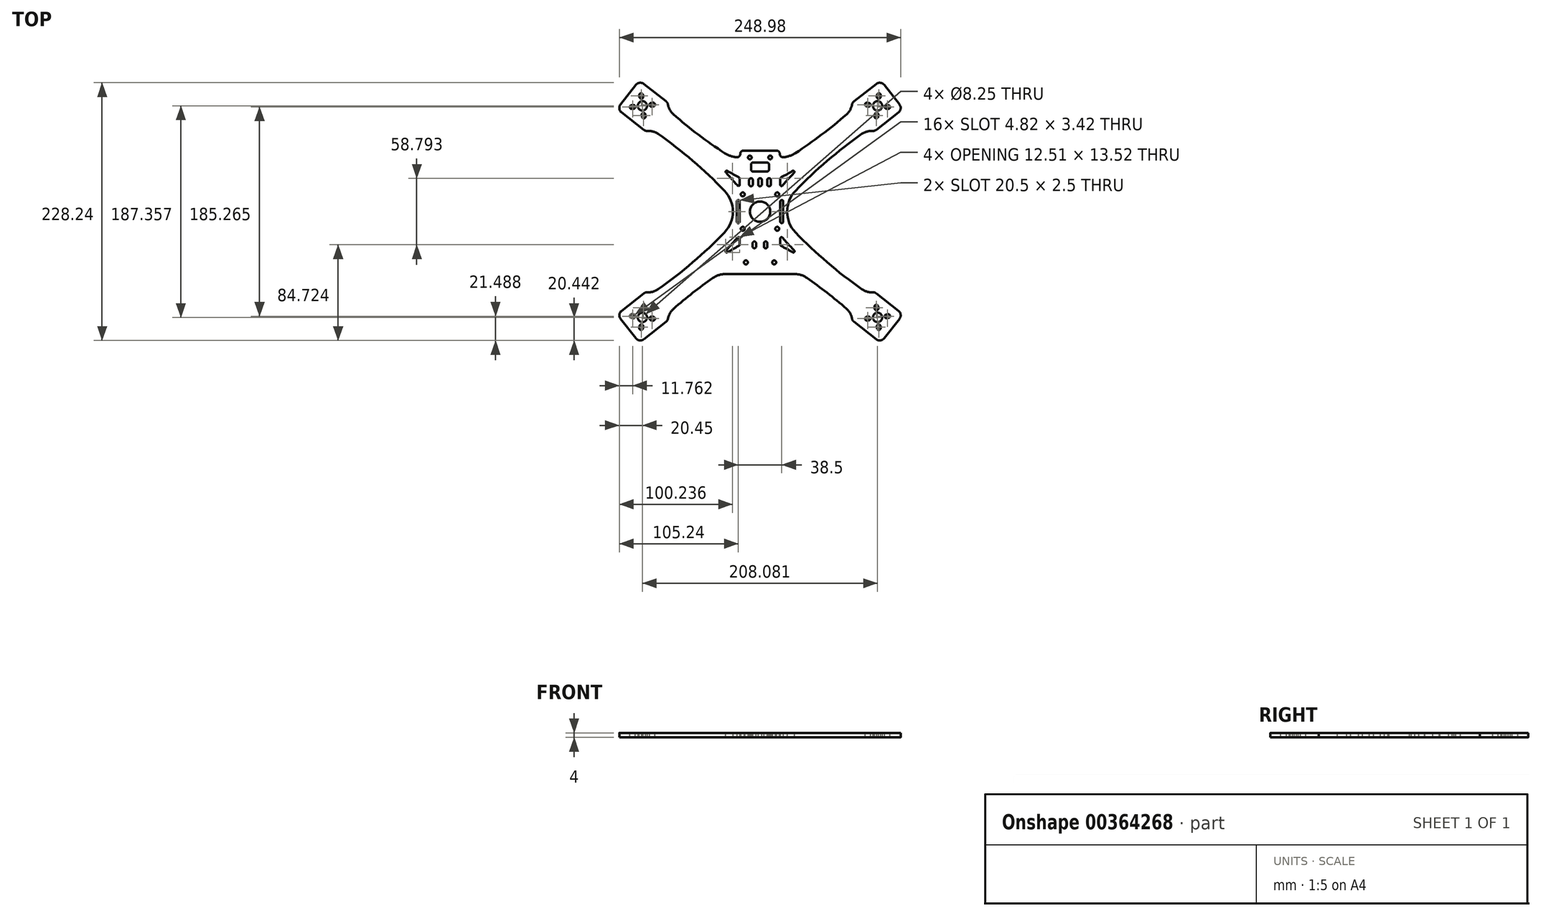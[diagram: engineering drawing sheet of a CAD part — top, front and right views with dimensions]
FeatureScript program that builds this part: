
annotation { "Feature Type Name" : "Feature", "Feature Type Description" : "" }
export const myFeature = defineFeature(function(context is Context, id is Id, definition is map)
    precondition{}
    {
        {
            var Q0;
            Q0=qCreatedBy(makeId("Top.planeOp"),FACE);
            var sketch = newSketch(context, id + "F0", { "sketchPlane" : qUnion([Q0])});
            skCircle(sketch, "E0", {"center": v(-15.25, 15.25) * mm, "radius": 1.75 * mm});
            skCircle(sketch, "E1", {"center": v(0, 0) * mm, "radius": 140 * mm, "construction": true});
            skCircle(sketch, "E2", {"center": v(-104.04, 93.68) * mm, "radius": 90 * mm, "construction": true});
            skLineSegment(sketch, "E3", {"start": v(0, 0) * mm, "end": v(-104.04, 93.68) * mm, "construction": true});
            skLineSegment(sketch, "E4", {"start": v(-104.04, 93.68) * mm, "end": v(0, 12) * mm, "construction": true});
            skLineSegment(sketch, "E5.bottom", {"start": v(-123.42, 94.9) * mm, "end": v(-109.83, 112.21) * mm});
            skLineSegment(sketch, "E5.left", {"start": v(-122.57, 87.89) * mm, "end": v(-102.95, 72.48) * mm});
            skLineSegment(sketch, "E5.right", {"start": v(-102.81, 113.06) * mm, "end": v(-83.2, 97.65) * mm});
            skLineSegment(sketch, "E6", {"start": v(-17.5, 54) * mm, "end": v(0, 54) * mm});
            skArc(sketch, "E7", {"start": v(-81.36, 94.62) * mm, "mid": v(-79.65, 89.9) * mm, "end": v(-76.48, 86.03) * mm});
            skArc(sketch, "E8", {"start": v(-90.07, 68.72) * mm, "mid": v(-94.59, 70.88) * mm, "end": v(-99.57, 71.42) * mm});
            skLineSegment(sketch, "E9", {"start": v(-19.25, 9) * mm, "end": v(-19.25, -9) * mm, "construction": true});
            skArc(sketch, "E10.0.startCap", {"start": v(-20.5, 9) * mm, "mid": v(-19.25, 10.25) * mm, "end": v(-18, 9) * mm});
            skArc(sketch, "E10.0.endCap", {"start": v(-18, -9) * mm, "mid": v(-19.25, -10.25) * mm, "end": v(-20.5, -9) * mm});
            skLineSegment(sketch, "E10.0.left", {"start": v(-18, 9) * mm, "end": v(-18, -9) * mm});
            skLineSegment(sketch, "E10.0.right", {"start": v(-20.5, 9) * mm, "end": v(-20.5, -9) * mm});
            skPoint(sketch, "E11.visualSharp", {"position": v(-126.5, 90.97) * mm});
            skArc(sketch, "E11.filletArc", {"start": v(-123.42, 94.9) * mm, "mid": v(-124.45, 91.22) * mm, "end": v(-122.57, 87.89) * mm});
            skPoint(sketch, "E12.visualSharp", {"position": v(-106.75, 116.14) * mm});
            skArc(sketch, "E12.filletArc", {"start": v(-102.81, 113.06) * mm, "mid": v(-106.5, 114.09) * mm, "end": v(-109.83, 112.21) * mm});
            skPoint(sketch, "E13.visualSharp", {"position": v(-101.34, 71.21) * mm});
            skArc(sketch, "E13.filletArc", {"start": v(-102.95, 72.48) * mm, "mid": v(-101.36, 71.64) * mm, "end": v(-99.57, 71.42) * mm});
            skPoint(sketch, "E14.visualSharp", {"position": v(-81.58, 96.38) * mm});
            skArc(sketch, "E14.filletArc", {"start": v(-81.36, 94.62) * mm, "mid": v(-82, 96.3) * mm, "end": v(-83.2, 97.65) * mm});
            skArc(sketch, "E15.MirrorCS", {"start": v(20.5, 9) * mm, "mid": v(19.25, 10.25) * mm, "end": v(18, 9) * mm});
            skArc(sketch, "E16.MirrorCS", {"start": v(81.36, 94.62) * mm, "mid": v(82, 96.3) * mm, "end": v(83.2, 97.65) * mm});
            skArc(sketch, "E17.MirrorCS", {"start": v(18, -9) * mm, "mid": v(19.25, -10.25) * mm, "end": v(20.5, -9) * mm});
            skArc(sketch, "E18.MirrorCS", {"start": v(102.95, 72.48) * mm, "mid": v(101.36, 71.64) * mm, "end": v(99.57, 71.42) * mm});
            skArc(sketch, "E19.MirrorCS", {"start": v(123.42, 94.9) * mm, "mid": v(124.45, 91.22) * mm, "end": v(122.57, 87.89) * mm});
            skArc(sketch, "E20.MirrorCS", {"start": v(81.36, 94.62) * mm, "mid": v(79.65, 89.9) * mm, "end": v(76.48, 86.03) * mm});
            skArc(sketch, "E21.MirrorCS", {"start": v(102.81, 113.06) * mm, "mid": v(106.5, 114.09) * mm, "end": v(109.83, 112.21) * mm});
            skArc(sketch, "E22.MirrorCS", {"start": v(90.07, 68.72) * mm, "mid": v(94.59, 70.88) * mm, "end": v(99.57, 71.42) * mm});
            skLineSegment(sketch, "E23.MirrorCS", {"start": v(20.5, 9) * mm, "end": v(20.5, -9) * mm});
            skLineSegment(sketch, "E24.MirrorCS", {"start": v(18, 9) * mm, "end": v(18, -9) * mm});
            skLineSegment(sketch, "E25.MirrorCS", {"start": v(19.25, 9) * mm, "end": v(19.25, -9) * mm, "construction": true});
            skLineSegment(sketch, "E26.MirrorCS", {"start": v(17.5, 54) * mm, "end": v(0, 54) * mm});
            skCircle(sketch, "E27.MirrorC", {"center": v(15.25, 15.25) * mm, "radius": 1.75 * mm});
            skPoint(sketch, "E28.MirrorP", {"position": v(81.58, 96.38) * mm});
            skLineSegment(sketch, "E29.MirrorCS", {"start": v(123.42, 94.9) * mm, "end": v(109.83, 112.21) * mm});
            skLineSegment(sketch, "E30.MirrorCS", {"start": v(0, 0) * mm, "end": v(104.04, 93.68) * mm, "construction": true});
            skLineSegment(sketch, "E31.MirrorCS", {"start": v(104.04, 93.68) * mm, "end": v(0, 12) * mm, "construction": true});
            skCircle(sketch, "E32.MirrorC", {"center": v(104.04, 93.68) * mm, "radius": 90 * mm, "construction": true});
            skLineSegment(sketch, "E33.MirrorCS", {"start": v(122.57, 87.89) * mm, "end": v(102.95, 72.48) * mm});
            skLineSegment(sketch, "E34.MirrorCS", {"start": v(102.81, 113.06) * mm, "end": v(83.2, 97.65) * mm});
            skPoint(sketch, "E35.MirrorP", {"position": v(106.75, 116.14) * mm});
            skPoint(sketch, "E36.MirrorP", {"position": v(101.34, 71.21) * mm});
            skPoint(sketch, "E37.MirrorP", {"position": v(126.5, 90.97) * mm});
            skArc(sketch, "E38.MirrorCS", {"start": v(-81.36, -94.62) * mm, "mid": v(-82, -96.3) * mm, "end": v(-83.2, -97.65) * mm});
            skArc(sketch, "E39.MirrorCS", {"start": v(-102.95, -72.48) * mm, "mid": v(-101.36, -71.64) * mm, "end": v(-99.57, -71.42) * mm});
            skArc(sketch, "E40.MirrorCS", {"start": v(81.36, -94.62) * mm, "mid": v(82, -96.3) * mm, "end": v(83.2, -97.65) * mm});
            skArc(sketch, "E41.MirrorCS", {"start": v(102.95, -72.48) * mm, "mid": v(101.36, -71.64) * mm, "end": v(99.57, -71.42) * mm});
            skArc(sketch, "E42.MirrorCS", {"start": v(90.07, -68.72) * mm, "mid": v(94.59, -70.88) * mm, "end": v(99.57, -71.42) * mm});
            skArc(sketch, "E43.MirrorCS", {"start": v(102.81, -113.06) * mm, "mid": v(106.5, -114.09) * mm, "end": v(109.83, -112.21) * mm});
            skArc(sketch, "E44.MirrorCS", {"start": v(-102.81, -113.06) * mm, "mid": v(-106.5, -114.09) * mm, "end": v(-109.83, -112.21) * mm});
            skArc(sketch, "E45.MirrorCS", {"start": v(-90.07, -68.72) * mm, "mid": v(-94.59, -70.88) * mm, "end": v(-99.57, -71.42) * mm});
            skArc(sketch, "E46.MirrorCS", {"start": v(-81.36, -94.62) * mm, "mid": v(-79.65, -89.9) * mm, "end": v(-76.48, -86.03) * mm});
            skArc(sketch, "E47.MirrorCS", {"start": v(123.42, -94.9) * mm, "mid": v(124.45, -91.22) * mm, "end": v(122.57, -87.89) * mm});
            skArc(sketch, "E48.MirrorCS", {"start": v(81.36, -94.62) * mm, "mid": v(79.65, -89.9) * mm, "end": v(76.48, -86.03) * mm});
            skArc(sketch, "E49.MirrorCS", {"start": v(-123.42, -94.9) * mm, "mid": v(-124.45, -91.22) * mm, "end": v(-122.57, -87.89) * mm});
            skCircle(sketch, "E50.MirrorC", {"center": v(-15.25, -15.25) * mm, "radius": 1.75 * mm});
            skCircle(sketch, "E51.MirrorC", {"center": v(15.25, -15.25) * mm, "radius": 1.75 * mm});
            skPoint(sketch, "E52.MirrorP", {"position": v(-81.58, -96.38) * mm});
            skLineSegment(sketch, "E53.MirrorCS", {"start": v(102.81, -113.06) * mm, "end": v(83.2, -97.65) * mm});
            skPoint(sketch, "E54.MirrorP", {"position": v(126.5, -90.97) * mm});
            skLineSegment(sketch, "E55.MirrorCS", {"start": v(122.57, -87.89) * mm, "end": v(102.95, -72.48) * mm});
            skPoint(sketch, "E56.MirrorP", {"position": v(101.34, -71.21) * mm});
            skPoint(sketch, "E57.MirrorP", {"position": v(-101.34, -71.21) * mm});
            skLineSegment(sketch, "E58.MirrorCS", {"start": v(-102.81, -113.06) * mm, "end": v(-83.2, -97.65) * mm});
            skLineSegment(sketch, "E59.MirrorCS", {"start": v(-122.57, -87.89) * mm, "end": v(-102.95, -72.48) * mm});
            skLineSegment(sketch, "E60.MirrorCS", {"start": v(-123.42, -94.9) * mm, "end": v(-109.83, -112.21) * mm});
            skPoint(sketch, "E61.MirrorP", {"position": v(-106.75, -116.14) * mm});
            skLineSegment(sketch, "E62.MirrorCS", {"start": v(123.42, -94.9) * mm, "end": v(109.83, -112.21) * mm});
            skPoint(sketch, "E63.MirrorP", {"position": v(106.75, -116.14) * mm});
            skPoint(sketch, "E64.MirrorP", {"position": v(-126.5, -90.97) * mm});
            skPoint(sketch, "E65.MirrorP", {"position": v(81.58, -96.38) * mm});
            skCircle(sketch, "E66.MirrorC", {"center": v(-104.04, -93.68) * mm, "radius": 90 * mm, "construction": true});
            skCircle(sketch, "E67.MirrorC", {"center": v(104.04, -93.68) * mm, "radius": 90 * mm, "construction": true});
            skCircle(sketch, "E68", {"center": v(-104.04, 93.68) * mm, "radius": 4.12 * mm});
            skCircle(sketch, "E69.MirrorC", {"center": v(104.04, 93.68) * mm, "radius": 4.12 * mm});
            skCircle(sketch, "E70.MirrorC", {"center": v(-104.04, -93.68) * mm, "radius": 4.12 * mm});
            skCircle(sketch, "E71.MirrorC", {"center": v(104.04, -93.68) * mm, "radius": 4.12 * mm});
            skArc(sketch, "E72", {"start": v(-31.4, 18.4) * mm, "mid": v(-59.52, 44.98) * mm, "end": v(-90.07, 68.72) * mm});
            skArc(sketch, "E73.MirrorCS", {"start": v(31.4, 18.4) * mm, "mid": v(59.52, 44.98) * mm, "end": v(90.07, 68.72) * mm});
            skArc(sketch, "E74.MirrorCS", {"start": v(-31.4, -18.4) * mm, "mid": v(-59.52, -44.98) * mm, "end": v(-90.07, -68.72) * mm});
            skArc(sketch, "E75.MirrorCS", {"start": v(31.4, -18.4) * mm, "mid": v(59.52, -44.98) * mm, "end": v(90.07, -68.72) * mm});
            skArc(sketch, "E76.trimOffspring", {"start": v(-31.27, 51.8) * mm, "mid": v(-54.48, 68.11) * mm, "end": v(-76.48, 86.03) * mm});
            skArc(sketch, "E77.MirrorCS", {"start": v(31.27, 51.8) * mm, "mid": v(54.48, 68.11) * mm, "end": v(76.48, 86.03) * mm});
            skArc(sketch, "E78.MirrorCS", {"start": v(41.71, -58.84) * mm, "mid": v(59.47, -71.95) * mm, "end": v(76.48, -86.03) * mm});
            skArc(sketch, "E79.MirrorCS", {"start": v(-41.71, -58.84) * mm, "mid": v(-59.47, -71.95) * mm, "end": v(-76.48, -86.03) * mm});
            skLineSegment(sketch, "E80", {"start": v(-30.28, -55.25) * mm, "end": v(30.28, -55.25) * mm});
            skPoint(sketch, "E81.visualSharp", {"position": v(-36.47, -55.25) * mm});
            skArc(sketch, "E81.filletArc", {"start": v(-30.28, -55.25) * mm, "mid": v(-36.27, -56.17) * mm, "end": v(-41.71, -58.84) * mm});
            skPoint(sketch, "E82.visualSharp", {"position": v(36.47, -55.25) * mm});
            skArc(sketch, "E82.filletArc", {"start": v(41.71, -58.84) * mm, "mid": v(36.27, -56.17) * mm, "end": v(30.28, -55.25) * mm});
            skArc(sketch, "E83.filletArc", {"start": v(-31.27, 51.8) * mm, "mid": v(-26.26, 49.33) * mm, "end": v(-20.8, 48.1) * mm});
            skArc(sketch, "E84.filletArc", {"start": v(20.8, 48.1) * mm, "mid": v(26.26, 49.33) * mm, "end": v(31.27, 51.8) * mm});
            skCircle(sketch, "E85", {"center": v(-9, 48) * mm, "radius": 1.63 * mm});
            skLineSegment(sketch, "E86", {"start": v(-17.5, 54) * mm, "end": v(-17.5, 51.1) * mm});
            skLineSegment(sketch, "E87", {"start": v(17.5, 54) * mm, "end": v(17.5, 51.1) * mm});
            skPoint(sketch, "E88.visualSharp", {"position": v(-17.5, 48) * mm});
            skArc(sketch, "E88.filletArc", {"start": v(-20.8, 48.1) * mm, "mid": v(-18.49, 48.86) * mm, "end": v(-17.5, 51.1) * mm});
            skPoint(sketch, "E89.visualSharp", {"position": v(17.5, 48) * mm});
            skArc(sketch, "E89.filletArc", {"start": v(17.5, 51.1) * mm, "mid": v(18.49, 48.86) * mm, "end": v(20.8, 48.1) * mm});
            skCircle(sketch, "E90.MirrorC", {"center": v(9, 48) * mm, "radius": 1.63 * mm});
            skPoint(sketch, "E91.visualSharp", {"position": v(-14.8, 0) * mm});
            skArc(sketch, "E91.filletArc", {"start": v(-31.4, -18.4) * mm, "mid": v(-24, 0) * mm, "end": v(-31.4, 18.4) * mm});
            skPoint(sketch, "E92.visualSharp", {"position": v(14.8, 0) * mm});
            skArc(sketch, "E92.filletArc", {"start": v(31.4, 18.4) * mm, "mid": v(24, 0) * mm, "end": v(31.4, -18.4) * mm});
            skCircle(sketch, "E93", {"center": v(-12.5, -45) * mm, "radius": 1.75 * mm});
            skCircle(sketch, "E94.MirrorC", {"center": v(12.5, -45) * mm, "radius": 1.75 * mm});
            skSolve(sketch);
        }
        {
            var Q0;
            Q0=qSketchRegion(id+"F0",true);
            extrude(context, id + "F1", {"entities" : qUnion([Q0]), "depth" : 4 * mm});
        }
        {
            var Q0;
            Q0=makeQuery(id+"F1.opExtrude","CAP_FACE",FACE,{"disambiguationData":[OSD([sQuery(id+"F0.wireOp",EDGE,"E0"),sQuery(id+"F0.wireOp",EDGE,"bZv11kwC-7Zwh-qoiM-MuVD-QWfY3VRXTvEb"),sQuery(id+"F0.wireOp",EDGE,"Hg7IfRWj-3ALA-Ly6Y-QmXC-kUpIx1ZQ4bFj"),sQuery(id+"F0.wireOp",EDGE,"i2Ly1i0H-hUQD-DSDW-V0AA-PaiG6Uw8rzNW"),sQuery(id+"F0.wireOp",EDGE,"E5.bottom"),sQuery(id+"F0.wireOp",EDGE,"E5.left"),sQuery(id+"F0.wireOp",EDGE,"E5.right"),sQuery(id+"F0.wireOp",EDGE,"E7"),sQuery(id+"F0.wireOp",EDGE,"E8"),sQuery(id+"F0.wireOp",EDGE,"26a3e7e2-4a16-4030-acf8-3f1fbd5a5a34.filletArc"),sQuery(id+"F0.wireOp",EDGE,"E10.0.startCap"),sQuery(id+"F0.wireOp",EDGE,"E10.0.endCap"),sQuery(id+"F0.wireOp",EDGE,"E10.0.left"),sQuery(id+"F0.wireOp",EDGE,"E10.0.right"),sQuery(id+"F0.wireOp",EDGE,"E11.filletArc"),sQuery(id+"F0.wireOp",EDGE,"E12.filletArc"),sQuery(id+"F0.wireOp",EDGE,"E13.filletArc"),sQuery(id+"F0.wireOp",EDGE,"E14.filletArc"),sQuery(id+"F0.wireOp",EDGE,"E15.MirrorCS"),sQuery(id+"F0.wireOp",EDGE,"E16.MirrorCS"),sQuery(id+"F0.wireOp",EDGE,"E17.MirrorCS"),sQuery(id+"F0.wireOp",EDGE,"E18.MirrorCS"),sQuery(id+"F0.wireOp",EDGE,"E19.MirrorCS"),sQuery(id+"F0.wireOp",EDGE,"E20.MirrorCS"),sQuery(id+"F0.wireOp",EDGE,"b7ecff87-ac14-4935-8a3e-caa413c79c2e13.MirrorCS"),sQuery(id+"F0.wireOp",EDGE,"E21.MirrorCS"),sQuery(id+"F0.wireOp",EDGE,"E22.MirrorCS"),sQuery(id+"F0.wireOp",EDGE,"E23.MirrorCS"),sQuery(id+"F0.wireOp",EDGE,"E24.MirrorCS"),sQuery(id+"F0.wireOp",EDGE,"b7ecff87-ac14-4935-8a3e-caa413c79c2e23.MirrorCS"),sQuery(id+"F0.wireOp",EDGE,"E27.MirrorC"),sQuery(id+"F0.wireOp",EDGE,"E29.MirrorCS"),sQuery(id+"F0.wireOp",EDGE,"b7ecff87-ac14-4935-8a3e-caa413c79c2e29.MirrorCS"),sQuery(id+"F0.wireOp",EDGE,"E33.MirrorCS"),sQuery(id+"F0.wireOp",EDGE,"E34.MirrorCS"),sQuery(id+"F0.wireOp",EDGE,"b7ecff87-ac14-4935-8a3e-caa413c79c2e39.MirrorCS"),sQuery(id+"F0.wireOp",EDGE,"E38.MirrorCS"),sQuery(id+"F0.wireOp",EDGE,"E39.MirrorCS"),sQuery(id+"F0.wireOp",EDGE,"E40.MirrorCS"),sQuery(id+"F0.wireOp",EDGE,"E41.MirrorCS"),sQuery(id+"F0.wireOp",EDGE,"E42.MirrorCS"),sQuery(id+"F0.wireOp",EDGE,"E43.MirrorCS"),sQuery(id+"F0.wireOp",EDGE,"E44.MirrorCS"),sQuery(id+"F0.wireOp",EDGE,"E45.MirrorCS"),sQuery(id+"F0.wireOp",EDGE,"E46.MirrorCS"),sQuery(id+"F0.wireOp",EDGE,"E47.MirrorCS"),sQuery(id+"F0.wireOp",EDGE,"E48.MirrorCS"),sQuery(id+"F0.wireOp",EDGE,"E49.MirrorCS"),sQuery(id+"F0.wireOp",EDGE,"E50.MirrorC"),sQuery(id+"F0.wireOp",EDGE,"E51.MirrorC"),sQuery(id+"F0.wireOp",EDGE,"7b8357ce-6b81-4621-bb5f-09712327f37e37.MirrorCS"),sQuery(id+"F0.wireOp",EDGE,"E53.MirrorCS"),sQuery(id+"F0.wireOp",EDGE,"E55.MirrorCS"),sQuery(id+"F0.wireOp",EDGE,"E58.MirrorCS"),sQuery(id+"F0.wireOp",EDGE,"E59.MirrorCS"),sQuery(id+"F0.wireOp",EDGE,"E60.MirrorCS"),sQuery(id+"F0.wireOp",EDGE,"7b8357ce-6b81-4621-bb5f-09712327f37e49.MirrorCS"),sQuery(id+"F0.wireOp",EDGE,"7b8357ce-6b81-4621-bb5f-09712327f37e50.MirrorCS"),sQuery(id+"F0.wireOp",EDGE,"E62.MirrorCS"),sQuery(id+"F0.wireOp",EDGE,"7b8357ce-6b81-4621-bb5f-09712327f37e55.MirrorCS"),sQuery(id+"F0.wireOp",EDGE,"d83ce2ea-2607-4b6c-a04d-38c7ae4304c90.MirrorCS"),sQuery(id+"F0.wireOp",EDGE,"b69c18a7-e43b-42be-b145-92b5204aa2ed0.MirrorCS"),sQuery(id+"F0.wireOp",EDGE,"a0707623-7043-4475-b436-6124989390590.MirrorCS"),sQuery(id+"F0.wireOp",EDGE,"4f61c261-c1ce-4229-8802-2f54477ed9b20.MirrorCS"),sQuery(id+"F0.wireOp",EDGE,"PiAP6XZh-xq8d-wj9O-Epc7-kF4WUdjTUHBz"),sQuery(id+"F0.wireOp",EDGE,"26e37ba6-caeb-4f33-ab48-1d1fe7035cbd0.MirrorC"),sQuery(id+"F0.wireOp",EDGE,"2yan8IeJ-tOHB-Kgj5-MnLH-DyiSyil4pG3S"),sQuery(id+"F0.wireOp",EDGE,"gHJ05LQx-usyR-kV3a-hPzh-QXjW5T1wXW1p"),sQuery(id+"F0.wireOp",EDGE,"uchXSoDE-KjdM-uTwm-rJXX-9rzWfyOP3x4Z"),sQuery(id+"F0.wireOp",EDGE,"8eu2Gxre-rbZ0-mDo1-W97T-pc3IviFYihye"),sQuery(id+"F0.wireOp",EDGE,"eavqlNsN-eOFr-pDPr-DEgw-YRCTYlhg5u3t"),sQuery(id+"F0.wireOp",EDGE,"Bw8slYh4-NEub-OYFD-4ET6-0dd0G63bUOwi"),sQuery(id+"F0.wireOp",EDGE,"af94888a-cba0-45cd-aecc-a0270221dd82.trimOffspring"),sQuery(id+"F0.wireOp",EDGE,"36199e4a-d6a7-49c4-a502-27b3488fd5e6.filletArc"),sQuery(id+"F0.wireOp",EDGE,"9e30e6b1-65ef-4937-9bd8-18fed2c5f1090.MirrorCS"),sQuery(id+"F0.wireOp",EDGE,"31f30485-6f3e-4795-917b-55e225d339680.MirrorCS"),sQuery(id+"F0.wireOp",EDGE,"86aa6092-d3c3-42aa-99ce-90435510c5960.MirrorCS"),sQuery(id+"F0.wireOp",EDGE,"5a69975c-1d9b-4b23-809c-878e26df679d0.MirrorCS"),sQuery(id+"F0.wireOp",EDGE,"8025df49-7d22-4dba-957a-6396c4b11ce90.MirrorCS"),sQuery(id+"F0.wireOp",EDGE,"b23088bf-ab4c-4e44-9a43-da8ffa8499a00.MirrorCS"),sQuery(id+"F0.wireOp",EDGE,"d9780cfa-9ead-4347-a629-1b1a594d6e410.MirrorCS"),sQuery(id+"F0.wireOp",EDGE,"68fec51b-96b4-4918-b858-b07c475e679e0.MirrorCS"),sQuery(id+"F0.wireOp",EDGE,"b72a6ee6-5ab0-4ed6-be8f-ffada714514d0.MirrorCS"),sQuery(id+"F0.wireOp",EDGE,"8773bbf2-5ef2-485a-bde0-34addb67332b0.MirrorCS"),sQuery(id+"F0.wireOp",EDGE,"ce348970-fad1-4eb4-9c27-5204bf570fdb0.MirrorCS"),sQuery(id+"F0.wireOp",EDGE,"404c4f6d-7f85-4f91-8924-7a461248f6590.MirrorCS"),sQuery(id+"F0.wireOp",EDGE,"TJ6xSgkY-RBVc-ApbF-Rnxn-nYxT4uNRJTxX"),sQuery(id+"F0.wireOp",EDGE,"hn5H7zRm-rU73-VfAX-dvYv-k9Lax7dM8k8G"),sQuery(id+"F0.wireOp",EDGE,"UOzbpYJr-Rpqu-ZeE8-tXKC-t89DSqlBGB8Q"),sQuery(id+"F0.wireOp",EDGE,"YxJJHRqV-amlc-LN3y-haml-tisoirnnfRJY"),sQuery(id+"F0.wireOp",EDGE,"033e0fe7-d3c1-42f5-ae8f-adbb043379e8.filletArc"),sQuery(id+"F0.wireOp",EDGE,"afa99035-e99d-4a73-974f-5500cdf2138a.filletArc"),sQuery(id+"F0.wireOp",EDGE,"9i3ea3iE-3Dll-Ek6R-PhGe-V1XcnAEkodY1.bottom"),sQuery(id+"F0.wireOp",EDGE,"9i3ea3iE-3Dll-Ek6R-PhGe-V1XcnAEkodY1.left"),sQuery(id+"F0.wireOp",EDGE,"9i3ea3iE-3Dll-Ek6R-PhGe-V1XcnAEkodY1.right"),sQuery(id+"F0.wireOp",EDGE,"1382622d-cae2-4c61-9f5c-b8746732d9fe0.MirrorCS"),sQuery(id+"F0.wireOp",EDGE,"0d70f9a0-c1ad-434e-a495-165a5a764f960.MirrorCS"),sQuery(id+"F0.wireOp",EDGE,"1f8d5036-162d-4fc3-b441-7a8ab5cd179e0.MirrorCS"),sQuery(id+"F0.wireOp",EDGE,"Km0E7gO1-P8tX-SnyZ-vo1L-W35BEzFtr7vK"),sQuery(id+"F0.wireOp",EDGE,"4twT0r3F-PA9R-wz1e-iyg0-9RBk79VGwi7g"),sQuery(id+"F0.wireOp",EDGE,"14bccf5c-bb99-48c5-a73f-577480a40b4e0.MirrorCS"),sQuery(id+"F0.wireOp",EDGE,"a123c59d-a695-4b06-9137-5aaff9e2b4be0.MirrorCS"),sQuery(id+"F0.wireOp",EDGE,"E68"),sQuery(id+"F0.wireOp",EDGE,"E69.MirrorC"),sQuery(id+"F0.wireOp",EDGE,"E70.MirrorC"),sQuery(id+"F0.wireOp",EDGE,"E71.MirrorC")])],"isStart":false});
            var sketch = newSketch(context, id + "F2", { "sketchPlane" : qUnion([Q0])});
            skCircle(sketch, "E95", {"center": v(-104.04, 93.68) * mm, "radius": 7.95 * mm, "construction": true});
            skCircle(sketch, "E96", {"center": v(-104.04, 93.68) * mm, "radius": 9.55 * mm, "construction": true});
            skLineSegment(sketch, "E97", {"start": v(-105, 101.57) * mm, "end": v(-105.18, 103.16) * mm, "construction": true});
            skLineSegment(sketch, "E98", {"start": v(-105, 101.57) * mm, "end": v(-104.04, 93.68) * mm, "construction": true});
            skLineSegment(sketch, "E99", {"start": v(-104.04, 93.68) * mm, "end": v(0, 12) * mm, "construction": true});
            skArc(sketch, "E100.0.startCap", {"start": v(-103.38, 101.77) * mm, "mid": v(-104.8, 99.96) * mm, "end": v(-106.6, 101.38) * mm});
            skArc(sketch, "E100.0.endCap", {"start": v(-106.8, 102.97) * mm, "mid": v(-105.38, 104.77) * mm, "end": v(-103.57, 103.35) * mm});
            skLineSegment(sketch, "E100.0.left", {"start": v(-106.6, 101.38) * mm, "end": v(-106.8, 102.97) * mm});
            skLineSegment(sketch, "E100.0.right", {"start": v(-103.38, 101.77) * mm, "end": v(-103.57, 103.35) * mm});
            skLineSegment(sketch, "E101.1.0", {"start": v(-111.93, 92.73) * mm, "end": v(-113.52, 92.54) * mm, "construction": true});
            skArc(sketch, "E101.1.1", {"start": v(-112.13, 94.34) * mm, "mid": v(-110.32, 92.92) * mm, "end": v(-111.74, 91.11) * mm});
            skLineSegment(sketch, "E101.1.2", {"start": v(-111.74, 91.11) * mm, "end": v(-113.33, 90.92) * mm});
            skLineSegment(sketch, "E101.1.3", {"start": v(-112.13, 94.34) * mm, "end": v(-113.72, 94.15) * mm});
            skArc(sketch, "E101.1.4", {"start": v(-113.33, 90.92) * mm, "mid": v(-115.14, 92.34) * mm, "end": v(-113.72, 94.15) * mm});
            skLineSegment(sketch, "E101.2.0", {"start": v(-103.09, 85.79) * mm, "end": v(-102.9, 84.2) * mm, "construction": true});
            skArc(sketch, "E101.2.1", {"start": v(-104.7, 85.6) * mm, "mid": v(-103.28, 87.4) * mm, "end": v(-101.48, 85.98) * mm});
            skLineSegment(sketch, "E101.2.2", {"start": v(-101.48, 85.98) * mm, "end": v(-101.29, 84.4) * mm});
            skLineSegment(sketch, "E101.2.3", {"start": v(-104.7, 85.6) * mm, "end": v(-104.51, 84) * mm});
            skArc(sketch, "E101.2.4", {"start": v(-101.29, 84.4) * mm, "mid": v(-102.7, 82.58) * mm, "end": v(-104.51, 84) * mm});
            skLineSegment(sketch, "E101.3.0", {"start": v(-96.15, 94.63) * mm, "end": v(-94.56, 94.82) * mm, "construction": true});
            skArc(sketch, "E101.3.1", {"start": v(-95.95, 93.02) * mm, "mid": v(-97.76, 94.43) * mm, "end": v(-96.34, 96.24) * mm});
            skLineSegment(sketch, "E101.3.2", {"start": v(-96.34, 96.24) * mm, "end": v(-94.75, 96.43) * mm});
            skLineSegment(sketch, "E101.3.3", {"start": v(-95.95, 93.02) * mm, "end": v(-94.36, 93.2) * mm});
            skArc(sketch, "E101.3.4", {"start": v(-94.75, 96.43) * mm, "mid": v(-92.95, 95.01) * mm, "end": v(-94.36, 93.2) * mm});
            skLineSegment(sketch, "E102.MirrorCS", {"start": v(105, 101.57) * mm, "end": v(105.18, 103.16) * mm, "construction": true});
            skLineSegment(sketch, "E103.MirrorCS", {"start": v(103.38, 101.77) * mm, "end": v(103.57, 103.35) * mm});
            skLineSegment(sketch, "E104.MirrorCS", {"start": v(111.93, 92.73) * mm, "end": v(113.52, 92.54) * mm, "construction": true});
            skLineSegment(sketch, "E105.MirrorCS", {"start": v(112.13, 94.34) * mm, "end": v(113.72, 94.15) * mm});
            skLineSegment(sketch, "E106.MirrorCS", {"start": v(96.34, 96.24) * mm, "end": v(94.75, 96.43) * mm});
            skLineSegment(sketch, "E107.MirrorCS", {"start": v(106.6, 101.38) * mm, "end": v(106.8, 102.97) * mm});
            skLineSegment(sketch, "E108.MirrorCS", {"start": v(104.7, 85.6) * mm, "end": v(104.51, 84) * mm});
            skLineSegment(sketch, "E109.MirrorCS", {"start": v(95.95, 93.02) * mm, "end": v(94.36, 93.2) * mm});
            skArc(sketch, "E110.MirrorCS", {"start": v(112.13, 94.34) * mm, "mid": v(110.32, 92.92) * mm, "end": v(111.74, 91.11) * mm});
            skArc(sketch, "E111.MirrorCS", {"start": v(106.8, 102.97) * mm, "mid": v(105.38, 104.77) * mm, "end": v(103.57, 103.35) * mm});
            skArc(sketch, "E112.MirrorCS", {"start": v(101.29, 84.4) * mm, "mid": v(102.7, 82.58) * mm, "end": v(104.51, 84) * mm});
            skLineSegment(sketch, "E113.MirrorCS", {"start": v(103.09, 85.79) * mm, "end": v(102.9, 84.2) * mm, "construction": true});
            skArc(sketch, "E114.MirrorCS", {"start": v(94.75, 96.43) * mm, "mid": v(92.95, 95.01) * mm, "end": v(94.36, 93.2) * mm});
            skArc(sketch, "E115.MirrorCS", {"start": v(113.33, 90.92) * mm, "mid": v(115.14, 92.34) * mm, "end": v(113.72, 94.15) * mm});
            skLineSegment(sketch, "E116.MirrorCS", {"start": v(96.15, 94.63) * mm, "end": v(94.56, 94.82) * mm, "construction": true});
            skLineSegment(sketch, "E117.MirrorCS", {"start": v(111.74, 91.11) * mm, "end": v(113.33, 90.92) * mm});
            skArc(sketch, "E118.MirrorCS", {"start": v(104.7, 85.6) * mm, "mid": v(103.28, 87.4) * mm, "end": v(101.48, 85.98) * mm});
            skArc(sketch, "E119.MirrorCS", {"start": v(95.95, 93.02) * mm, "mid": v(97.76, 94.43) * mm, "end": v(96.34, 96.24) * mm});
            skLineSegment(sketch, "E120.MirrorCS", {"start": v(101.48, 85.98) * mm, "end": v(101.29, 84.4) * mm});
            skArc(sketch, "E121.MirrorCS", {"start": v(103.38, 101.77) * mm, "mid": v(104.8, 99.96) * mm, "end": v(106.6, 101.38) * mm});
            skPoint(sketch, "E122.MirrorP", {"position": v(104.04, 93.68) * mm});
            skCircle(sketch, "E123.MirrorC", {"center": v(104.04, 93.68) * mm, "radius": 9.55 * mm, "construction": true});
            skCircle(sketch, "E124.MirrorC", {"center": v(104.04, 93.68) * mm, "radius": 7.95 * mm, "construction": true});
            skLineSegment(sketch, "E125.MirrorCS", {"start": v(105, 101.57) * mm, "end": v(104.04, 93.68) * mm, "construction": true});
            skLineSegment(sketch, "E126.MirrorCS", {"start": v(-105, -101.57) * mm, "end": v(-105.18, -103.16) * mm, "construction": true});
            skLineSegment(sketch, "E127.MirrorCS", {"start": v(-103.38, -101.77) * mm, "end": v(-103.57, -103.35) * mm});
            skArc(sketch, "E128.MirrorCS", {"start": v(-103.38, -101.77) * mm, "mid": v(-104.8, -99.96) * mm, "end": v(-106.6, -101.38) * mm});
            skLineSegment(sketch, "E129.MirrorCS", {"start": v(-105, -101.57) * mm, "end": v(-104.04, -93.68) * mm, "construction": true});
            skLineSegment(sketch, "E130.MirrorCS", {"start": v(-106.6, -101.38) * mm, "end": v(-106.8, -102.97) * mm});
            skLineSegment(sketch, "E131.MirrorCS", {"start": v(-112.13, -94.34) * mm, "end": v(-113.72, -94.15) * mm});
            skLineSegment(sketch, "E132.MirrorCS", {"start": v(95.95, -93.02) * mm, "end": v(94.36, -93.2) * mm});
            skArc(sketch, "E133.MirrorCS", {"start": v(95.95, -93.02) * mm, "mid": v(97.76, -94.43) * mm, "end": v(96.34, -96.24) * mm});
            skLineSegment(sketch, "E134.MirrorCS", {"start": v(106.6, -101.38) * mm, "end": v(106.8, -102.97) * mm});
            skArc(sketch, "E135.MirrorCS", {"start": v(-112.13, -94.34) * mm, "mid": v(-110.32, -92.92) * mm, "end": v(-111.74, -91.11) * mm});
            skLineSegment(sketch, "E136.MirrorCS", {"start": v(-111.74, -91.11) * mm, "end": v(-113.33, -90.92) * mm});
            skLineSegment(sketch, "E137.MirrorCS", {"start": v(-111.93, -92.73) * mm, "end": v(-113.52, -92.54) * mm, "construction": true});
            skArc(sketch, "E138.MirrorCS", {"start": v(-113.33, -90.92) * mm, "mid": v(-115.14, -92.34) * mm, "end": v(-113.72, -94.15) * mm});
            skLineSegment(sketch, "E139.MirrorCS", {"start": v(111.93, -92.73) * mm, "end": v(113.52, -92.54) * mm, "construction": true});
            skLineSegment(sketch, "E140.MirrorCS", {"start": v(96.15, -94.63) * mm, "end": v(94.56, -94.82) * mm, "construction": true});
            skLineSegment(sketch, "E141.MirrorCS", {"start": v(111.74, -91.11) * mm, "end": v(113.33, -90.92) * mm});
            skArc(sketch, "E142.MirrorCS", {"start": v(112.13, -94.34) * mm, "mid": v(110.32, -92.92) * mm, "end": v(111.74, -91.11) * mm});
            skLineSegment(sketch, "E143.MirrorCS", {"start": v(96.34, -96.24) * mm, "end": v(94.75, -96.43) * mm});
            skArc(sketch, "E144.MirrorCS", {"start": v(103.38, -101.77) * mm, "mid": v(104.8, -99.96) * mm, "end": v(106.6, -101.38) * mm});
            skLineSegment(sketch, "E145.MirrorCS", {"start": v(103.38, -101.77) * mm, "end": v(103.57, -103.35) * mm});
            skLineSegment(sketch, "E146.MirrorCS", {"start": v(112.13, -94.34) * mm, "end": v(113.72, -94.15) * mm});
            skArc(sketch, "E147.MirrorCS", {"start": v(113.33, -90.92) * mm, "mid": v(115.14, -92.34) * mm, "end": v(113.72, -94.15) * mm});
            skLineSegment(sketch, "E148.MirrorCS", {"start": v(105, -101.57) * mm, "end": v(104.04, -93.68) * mm, "construction": true});
            skLineSegment(sketch, "E149.MirrorCS", {"start": v(105, -101.57) * mm, "end": v(105.18, -103.16) * mm, "construction": true});
            skLineSegment(sketch, "E150.MirrorCS", {"start": v(101.48, -85.98) * mm, "end": v(101.29, -84.4) * mm});
            skLineSegment(sketch, "E151.MirrorCS", {"start": v(-101.48, -85.98) * mm, "end": v(-101.29, -84.4) * mm});
            skLineSegment(sketch, "E152.MirrorCS", {"start": v(-104.7, -85.6) * mm, "end": v(-104.51, -84) * mm});
            skArc(sketch, "E153.MirrorCS", {"start": v(-94.75, -96.43) * mm, "mid": v(-92.95, -95.01) * mm, "end": v(-94.36, -93.2) * mm});
            skArc(sketch, "E154.MirrorCS", {"start": v(106.8, -102.97) * mm, "mid": v(105.38, -104.77) * mm, "end": v(103.57, -103.35) * mm});
            skArc(sketch, "E155.MirrorCS", {"start": v(104.7, -85.6) * mm, "mid": v(103.28, -87.4) * mm, "end": v(101.48, -85.98) * mm});
            skArc(sketch, "E156.MirrorCS", {"start": v(-101.29, -84.4) * mm, "mid": v(-102.7, -82.58) * mm, "end": v(-104.51, -84) * mm});
            skLineSegment(sketch, "E157.MirrorCS", {"start": v(-96.34, -96.24) * mm, "end": v(-94.75, -96.43) * mm});
            skArc(sketch, "E158.MirrorCS", {"start": v(-95.95, -93.02) * mm, "mid": v(-97.76, -94.43) * mm, "end": v(-96.34, -96.24) * mm});
            skArc(sketch, "E159.MirrorCS", {"start": v(-106.8, -102.97) * mm, "mid": v(-105.38, -104.77) * mm, "end": v(-103.57, -103.35) * mm});
            skArc(sketch, "E160.MirrorCS", {"start": v(101.29, -84.4) * mm, "mid": v(102.7, -82.58) * mm, "end": v(104.51, -84) * mm});
            skLineSegment(sketch, "E161.MirrorCS", {"start": v(-96.15, -94.63) * mm, "end": v(-94.56, -94.82) * mm, "construction": true});
            skArc(sketch, "E162.MirrorCS", {"start": v(94.75, -96.43) * mm, "mid": v(92.95, -95.01) * mm, "end": v(94.36, -93.2) * mm});
            skArc(sketch, "E163.MirrorCS", {"start": v(-104.7, -85.6) * mm, "mid": v(-103.28, -87.4) * mm, "end": v(-101.48, -85.98) * mm});
            skLineSegment(sketch, "E164.MirrorCS", {"start": v(-95.95, -93.02) * mm, "end": v(-94.36, -93.2) * mm});
            skLineSegment(sketch, "E165.MirrorCS", {"start": v(104.7, -85.6) * mm, "end": v(104.51, -84) * mm});
            skLineSegment(sketch, "E166.MirrorCS", {"start": v(103.09, -85.79) * mm, "end": v(102.9, -84.2) * mm, "construction": true});
            skLineSegment(sketch, "E167.MirrorCS", {"start": v(-103.09, -85.79) * mm, "end": v(-102.9, -84.2) * mm, "construction": true});
            skCircle(sketch, "E168.MirrorC", {"center": v(104.04, -93.68) * mm, "radius": 7.95 * mm, "construction": true});
            skCircle(sketch, "E169.MirrorC", {"center": v(-104.04, -93.68) * mm, "radius": 7.95 * mm, "construction": true});
            skCircle(sketch, "E170.MirrorC", {"center": v(-104.04, -93.68) * mm, "radius": 9.55 * mm, "construction": true});
            skCircle(sketch, "E171.MirrorC", {"center": v(104.04, -93.68) * mm, "radius": 9.55 * mm, "construction": true});
            skSolve(sketch);
        }
        {
            var Q0;
            Q0=qSketchRegion(id+"F2",true);
            extrude(context, id + "F3", {"entities" : qUnion([Q0]), "operationType" : NewBodyOperationType.REMOVE, "oppositeDirection" : true, "depth" : 25 * mm, "offsetDistance" : 25 * mm});
        }
        {
            var Q0;
            Q0=makeQuery(id+"F1.opExtrude","CAP_FACE",FACE,{"disambiguationData":[OSD([sQuery(id+"F0.wireOp",EDGE,"E0"),sQuery(id+"F0.wireOp",EDGE,"bZv11kwC-7Zwh-qoiM-MuVD-QWfY3VRXTvEb"),sQuery(id+"F0.wireOp",EDGE,"Hg7IfRWj-3ALA-Ly6Y-QmXC-kUpIx1ZQ4bFj"),sQuery(id+"F0.wireOp",EDGE,"i2Ly1i0H-hUQD-DSDW-V0AA-PaiG6Uw8rzNW"),sQuery(id+"F0.wireOp",EDGE,"E5.bottom"),sQuery(id+"F0.wireOp",EDGE,"E5.left"),sQuery(id+"F0.wireOp",EDGE,"E5.right"),sQuery(id+"F0.wireOp",EDGE,"E7"),sQuery(id+"F0.wireOp",EDGE,"E8"),sQuery(id+"F0.wireOp",EDGE,"26a3e7e2-4a16-4030-acf8-3f1fbd5a5a34.filletArc"),sQuery(id+"F0.wireOp",EDGE,"E10.0.startCap"),sQuery(id+"F0.wireOp",EDGE,"E10.0.endCap"),sQuery(id+"F0.wireOp",EDGE,"E10.0.left"),sQuery(id+"F0.wireOp",EDGE,"E10.0.right"),sQuery(id+"F0.wireOp",EDGE,"E11.filletArc"),sQuery(id+"F0.wireOp",EDGE,"E12.filletArc"),sQuery(id+"F0.wireOp",EDGE,"E13.filletArc"),sQuery(id+"F0.wireOp",EDGE,"E14.filletArc"),sQuery(id+"F0.wireOp",EDGE,"E15.MirrorCS"),sQuery(id+"F0.wireOp",EDGE,"E16.MirrorCS"),sQuery(id+"F0.wireOp",EDGE,"E17.MirrorCS"),sQuery(id+"F0.wireOp",EDGE,"E18.MirrorCS"),sQuery(id+"F0.wireOp",EDGE,"E19.MirrorCS"),sQuery(id+"F0.wireOp",EDGE,"E20.MirrorCS"),sQuery(id+"F0.wireOp",EDGE,"b7ecff87-ac14-4935-8a3e-caa413c79c2e13.MirrorCS"),sQuery(id+"F0.wireOp",EDGE,"E21.MirrorCS"),sQuery(id+"F0.wireOp",EDGE,"E22.MirrorCS"),sQuery(id+"F0.wireOp",EDGE,"E23.MirrorCS"),sQuery(id+"F0.wireOp",EDGE,"E24.MirrorCS"),sQuery(id+"F0.wireOp",EDGE,"b7ecff87-ac14-4935-8a3e-caa413c79c2e23.MirrorCS"),sQuery(id+"F0.wireOp",EDGE,"E27.MirrorC"),sQuery(id+"F0.wireOp",EDGE,"E29.MirrorCS"),sQuery(id+"F0.wireOp",EDGE,"b7ecff87-ac14-4935-8a3e-caa413c79c2e29.MirrorCS"),sQuery(id+"F0.wireOp",EDGE,"E33.MirrorCS"),sQuery(id+"F0.wireOp",EDGE,"E34.MirrorCS"),sQuery(id+"F0.wireOp",EDGE,"b7ecff87-ac14-4935-8a3e-caa413c79c2e39.MirrorCS"),sQuery(id+"F0.wireOp",EDGE,"E38.MirrorCS"),sQuery(id+"F0.wireOp",EDGE,"E39.MirrorCS"),sQuery(id+"F0.wireOp",EDGE,"E40.MirrorCS"),sQuery(id+"F0.wireOp",EDGE,"E41.MirrorCS"),sQuery(id+"F0.wireOp",EDGE,"E42.MirrorCS"),sQuery(id+"F0.wireOp",EDGE,"E43.MirrorCS"),sQuery(id+"F0.wireOp",EDGE,"E44.MirrorCS"),sQuery(id+"F0.wireOp",EDGE,"E45.MirrorCS"),sQuery(id+"F0.wireOp",EDGE,"E46.MirrorCS"),sQuery(id+"F0.wireOp",EDGE,"E47.MirrorCS"),sQuery(id+"F0.wireOp",EDGE,"E48.MirrorCS"),sQuery(id+"F0.wireOp",EDGE,"E49.MirrorCS"),sQuery(id+"F0.wireOp",EDGE,"E50.MirrorC"),sQuery(id+"F0.wireOp",EDGE,"E51.MirrorC"),sQuery(id+"F0.wireOp",EDGE,"7b8357ce-6b81-4621-bb5f-09712327f37e37.MirrorCS"),sQuery(id+"F0.wireOp",EDGE,"E53.MirrorCS"),sQuery(id+"F0.wireOp",EDGE,"E55.MirrorCS"),sQuery(id+"F0.wireOp",EDGE,"E58.MirrorCS"),sQuery(id+"F0.wireOp",EDGE,"E59.MirrorCS"),sQuery(id+"F0.wireOp",EDGE,"E60.MirrorCS"),sQuery(id+"F0.wireOp",EDGE,"7b8357ce-6b81-4621-bb5f-09712327f37e49.MirrorCS"),sQuery(id+"F0.wireOp",EDGE,"7b8357ce-6b81-4621-bb5f-09712327f37e50.MirrorCS"),sQuery(id+"F0.wireOp",EDGE,"E62.MirrorCS"),sQuery(id+"F0.wireOp",EDGE,"7b8357ce-6b81-4621-bb5f-09712327f37e55.MirrorCS"),sQuery(id+"F0.wireOp",EDGE,"d83ce2ea-2607-4b6c-a04d-38c7ae4304c90.MirrorCS"),sQuery(id+"F0.wireOp",EDGE,"b69c18a7-e43b-42be-b145-92b5204aa2ed0.MirrorCS"),sQuery(id+"F0.wireOp",EDGE,"a0707623-7043-4475-b436-6124989390590.MirrorCS"),sQuery(id+"F0.wireOp",EDGE,"4f61c261-c1ce-4229-8802-2f54477ed9b20.MirrorCS"),sQuery(id+"F0.wireOp",EDGE,"PiAP6XZh-xq8d-wj9O-Epc7-kF4WUdjTUHBz"),sQuery(id+"F0.wireOp",EDGE,"26e37ba6-caeb-4f33-ab48-1d1fe7035cbd0.MirrorC"),sQuery(id+"F0.wireOp",EDGE,"2yan8IeJ-tOHB-Kgj5-MnLH-DyiSyil4pG3S"),sQuery(id+"F0.wireOp",EDGE,"gHJ05LQx-usyR-kV3a-hPzh-QXjW5T1wXW1p"),sQuery(id+"F0.wireOp",EDGE,"uchXSoDE-KjdM-uTwm-rJXX-9rzWfyOP3x4Z"),sQuery(id+"F0.wireOp",EDGE,"8eu2Gxre-rbZ0-mDo1-W97T-pc3IviFYihye"),sQuery(id+"F0.wireOp",EDGE,"eavqlNsN-eOFr-pDPr-DEgw-YRCTYlhg5u3t"),sQuery(id+"F0.wireOp",EDGE,"Bw8slYh4-NEub-OYFD-4ET6-0dd0G63bUOwi"),sQuery(id+"F0.wireOp",EDGE,"af94888a-cba0-45cd-aecc-a0270221dd82.trimOffspring"),sQuery(id+"F0.wireOp",EDGE,"36199e4a-d6a7-49c4-a502-27b3488fd5e6.filletArc"),sQuery(id+"F0.wireOp",EDGE,"9e30e6b1-65ef-4937-9bd8-18fed2c5f1090.MirrorCS"),sQuery(id+"F0.wireOp",EDGE,"31f30485-6f3e-4795-917b-55e225d339680.MirrorCS"),sQuery(id+"F0.wireOp",EDGE,"86aa6092-d3c3-42aa-99ce-90435510c5960.MirrorCS"),sQuery(id+"F0.wireOp",EDGE,"5a69975c-1d9b-4b23-809c-878e26df679d0.MirrorCS"),sQuery(id+"F0.wireOp",EDGE,"8025df49-7d22-4dba-957a-6396c4b11ce90.MirrorCS"),sQuery(id+"F0.wireOp",EDGE,"b23088bf-ab4c-4e44-9a43-da8ffa8499a00.MirrorCS"),sQuery(id+"F0.wireOp",EDGE,"d9780cfa-9ead-4347-a629-1b1a594d6e410.MirrorCS"),sQuery(id+"F0.wireOp",EDGE,"68fec51b-96b4-4918-b858-b07c475e679e0.MirrorCS"),sQuery(id+"F0.wireOp",EDGE,"b72a6ee6-5ab0-4ed6-be8f-ffada714514d0.MirrorCS"),sQuery(id+"F0.wireOp",EDGE,"8773bbf2-5ef2-485a-bde0-34addb67332b0.MirrorCS"),sQuery(id+"F0.wireOp",EDGE,"ce348970-fad1-4eb4-9c27-5204bf570fdb0.MirrorCS"),sQuery(id+"F0.wireOp",EDGE,"404c4f6d-7f85-4f91-8924-7a461248f6590.MirrorCS"),sQuery(id+"F0.wireOp",EDGE,"TJ6xSgkY-RBVc-ApbF-Rnxn-nYxT4uNRJTxX"),sQuery(id+"F0.wireOp",EDGE,"hn5H7zRm-rU73-VfAX-dvYv-k9Lax7dM8k8G"),sQuery(id+"F0.wireOp",EDGE,"UOzbpYJr-Rpqu-ZeE8-tXKC-t89DSqlBGB8Q"),sQuery(id+"F0.wireOp",EDGE,"YxJJHRqV-amlc-LN3y-haml-tisoirnnfRJY"),sQuery(id+"F0.wireOp",EDGE,"033e0fe7-d3c1-42f5-ae8f-adbb043379e8.filletArc"),sQuery(id+"F0.wireOp",EDGE,"afa99035-e99d-4a73-974f-5500cdf2138a.filletArc"),sQuery(id+"F0.wireOp",EDGE,"9i3ea3iE-3Dll-Ek6R-PhGe-V1XcnAEkodY1.bottom"),sQuery(id+"F0.wireOp",EDGE,"9i3ea3iE-3Dll-Ek6R-PhGe-V1XcnAEkodY1.left"),sQuery(id+"F0.wireOp",EDGE,"9i3ea3iE-3Dll-Ek6R-PhGe-V1XcnAEkodY1.right"),sQuery(id+"F0.wireOp",EDGE,"1382622d-cae2-4c61-9f5c-b8746732d9fe0.MirrorCS"),sQuery(id+"F0.wireOp",EDGE,"0d70f9a0-c1ad-434e-a495-165a5a764f960.MirrorCS"),sQuery(id+"F0.wireOp",EDGE,"1f8d5036-162d-4fc3-b441-7a8ab5cd179e0.MirrorCS"),sQuery(id+"F0.wireOp",EDGE,"Km0E7gO1-P8tX-SnyZ-vo1L-W35BEzFtr7vK"),sQuery(id+"F0.wireOp",EDGE,"4twT0r3F-PA9R-wz1e-iyg0-9RBk79VGwi7g"),sQuery(id+"F0.wireOp",EDGE,"14bccf5c-bb99-48c5-a73f-577480a40b4e0.MirrorCS"),sQuery(id+"F0.wireOp",EDGE,"a123c59d-a695-4b06-9137-5aaff9e2b4be0.MirrorCS"),sQuery(id+"F0.wireOp",EDGE,"E68"),sQuery(id+"F0.wireOp",EDGE,"E69.MirrorC"),sQuery(id+"F0.wireOp",EDGE,"E70.MirrorC"),sQuery(id+"F0.wireOp",EDGE,"E71.MirrorC")])],"isStart":false});
            var sketch = newSketch(context, id + "F4", { "sketchPlane" : qUnion([Q0])});
            skLineSegment(sketch, "E172", {"start": v(0, 28) * mm, "end": v(0, 24) * mm, "construction": true});
            skLineSegment(sketch, "E173", {"start": v(-8, 28) * mm, "end": v(-8, 24) * mm, "construction": true});
            skLineSegment(sketch, "E174.MirrorCS", {"start": v(8, 28) * mm, "end": v(8, 24) * mm, "construction": true});
            skArc(sketch, "E175.0.startCap", {"start": v(-9.62, 28) * mm, "mid": v(-8, 29.62) * mm, "end": v(-6.38, 28) * mm});
            skArc(sketch, "E175.0.endCap", {"start": v(-6.38, 24) * mm, "mid": v(-8, 22.38) * mm, "end": v(-9.62, 24) * mm});
            skLineSegment(sketch, "E175.0.left", {"start": v(-6.38, 28) * mm, "end": v(-6.38, 24) * mm});
            skLineSegment(sketch, "E175.0.right", {"start": v(-9.62, 28) * mm, "end": v(-9.62, 24) * mm});
            skArc(sketch, "E175.1.startCap", {"start": v(-1.63, 28) * mm, "mid": v(0, 29.63) * mm, "end": v(1.63, 28) * mm});
            skArc(sketch, "E175.1.endCap", {"start": v(1.63, 24) * mm, "mid": v(0, 22.38) * mm, "end": v(-1.63, 24) * mm});
            skLineSegment(sketch, "E175.1.left", {"start": v(1.63, 28) * mm, "end": v(1.63, 24) * mm});
            skLineSegment(sketch, "E175.1.right", {"start": v(-1.63, 28) * mm, "end": v(-1.63, 24) * mm});
            skArc(sketch, "E175.2.startCap", {"start": v(6.38, 28) * mm, "mid": v(8, 29.62) * mm, "end": v(9.62, 28) * mm});
            skArc(sketch, "E175.2.endCap", {"start": v(9.62, 24) * mm, "mid": v(8, 22.38) * mm, "end": v(6.38, 24) * mm});
            skLineSegment(sketch, "E175.2.left", {"start": v(9.62, 28) * mm, "end": v(9.62, 24) * mm});
            skLineSegment(sketch, "E175.2.right", {"start": v(6.38, 28) * mm, "end": v(6.38, 24) * mm});
            skSolve(sketch);
        }
        {
            var Q0;
            Q0=qSketchRegion(id+"F4",true);
            extrude(context, id + "F5", {"entities" : qUnion([Q0]), "operationType" : NewBodyOperationType.REMOVE, "oppositeDirection" : true, "depth" : 25 * mm, "offsetDistance" : 25 * mm});
        }
        {
            var Q0;
            Q0=makeQuery(id+"F1.opExtrude","CAP_FACE",FACE,{"disambiguationData":[OSD([sQuery(id+"F0.wireOp",EDGE,"E0"),sQuery(id+"F0.wireOp",EDGE,"bZv11kwC-7Zwh-qoiM-MuVD-QWfY3VRXTvEb"),sQuery(id+"F0.wireOp",EDGE,"Hg7IfRWj-3ALA-Ly6Y-QmXC-kUpIx1ZQ4bFj"),sQuery(id+"F0.wireOp",EDGE,"i2Ly1i0H-hUQD-DSDW-V0AA-PaiG6Uw8rzNW"),sQuery(id+"F0.wireOp",EDGE,"E5.bottom"),sQuery(id+"F0.wireOp",EDGE,"E5.left"),sQuery(id+"F0.wireOp",EDGE,"E5.right"),sQuery(id+"F0.wireOp",EDGE,"E7"),sQuery(id+"F0.wireOp",EDGE,"E8"),sQuery(id+"F0.wireOp",EDGE,"26a3e7e2-4a16-4030-acf8-3f1fbd5a5a34.filletArc"),sQuery(id+"F0.wireOp",EDGE,"E10.0.startCap"),sQuery(id+"F0.wireOp",EDGE,"E10.0.endCap"),sQuery(id+"F0.wireOp",EDGE,"E10.0.left"),sQuery(id+"F0.wireOp",EDGE,"E10.0.right"),sQuery(id+"F0.wireOp",EDGE,"E11.filletArc"),sQuery(id+"F0.wireOp",EDGE,"E12.filletArc"),sQuery(id+"F0.wireOp",EDGE,"E13.filletArc"),sQuery(id+"F0.wireOp",EDGE,"E14.filletArc"),sQuery(id+"F0.wireOp",EDGE,"E15.MirrorCS"),sQuery(id+"F0.wireOp",EDGE,"E16.MirrorCS"),sQuery(id+"F0.wireOp",EDGE,"E17.MirrorCS"),sQuery(id+"F0.wireOp",EDGE,"E18.MirrorCS"),sQuery(id+"F0.wireOp",EDGE,"E19.MirrorCS"),sQuery(id+"F0.wireOp",EDGE,"E20.MirrorCS"),sQuery(id+"F0.wireOp",EDGE,"b7ecff87-ac14-4935-8a3e-caa413c79c2e13.MirrorCS"),sQuery(id+"F0.wireOp",EDGE,"E21.MirrorCS"),sQuery(id+"F0.wireOp",EDGE,"E22.MirrorCS"),sQuery(id+"F0.wireOp",EDGE,"E23.MirrorCS"),sQuery(id+"F0.wireOp",EDGE,"E24.MirrorCS"),sQuery(id+"F0.wireOp",EDGE,"b7ecff87-ac14-4935-8a3e-caa413c79c2e23.MirrorCS"),sQuery(id+"F0.wireOp",EDGE,"E27.MirrorC"),sQuery(id+"F0.wireOp",EDGE,"E29.MirrorCS"),sQuery(id+"F0.wireOp",EDGE,"b7ecff87-ac14-4935-8a3e-caa413c79c2e29.MirrorCS"),sQuery(id+"F0.wireOp",EDGE,"E33.MirrorCS"),sQuery(id+"F0.wireOp",EDGE,"E34.MirrorCS"),sQuery(id+"F0.wireOp",EDGE,"b7ecff87-ac14-4935-8a3e-caa413c79c2e39.MirrorCS"),sQuery(id+"F0.wireOp",EDGE,"E38.MirrorCS"),sQuery(id+"F0.wireOp",EDGE,"E39.MirrorCS"),sQuery(id+"F0.wireOp",EDGE,"E40.MirrorCS"),sQuery(id+"F0.wireOp",EDGE,"E41.MirrorCS"),sQuery(id+"F0.wireOp",EDGE,"E42.MirrorCS"),sQuery(id+"F0.wireOp",EDGE,"E43.MirrorCS"),sQuery(id+"F0.wireOp",EDGE,"E44.MirrorCS"),sQuery(id+"F0.wireOp",EDGE,"E45.MirrorCS"),sQuery(id+"F0.wireOp",EDGE,"E46.MirrorCS"),sQuery(id+"F0.wireOp",EDGE,"E47.MirrorCS"),sQuery(id+"F0.wireOp",EDGE,"E48.MirrorCS"),sQuery(id+"F0.wireOp",EDGE,"E49.MirrorCS"),sQuery(id+"F0.wireOp",EDGE,"E50.MirrorC"),sQuery(id+"F0.wireOp",EDGE,"E51.MirrorC"),sQuery(id+"F0.wireOp",EDGE,"7b8357ce-6b81-4621-bb5f-09712327f37e37.MirrorCS"),sQuery(id+"F0.wireOp",EDGE,"E53.MirrorCS"),sQuery(id+"F0.wireOp",EDGE,"E55.MirrorCS"),sQuery(id+"F0.wireOp",EDGE,"E58.MirrorCS"),sQuery(id+"F0.wireOp",EDGE,"E59.MirrorCS"),sQuery(id+"F0.wireOp",EDGE,"E60.MirrorCS"),sQuery(id+"F0.wireOp",EDGE,"7b8357ce-6b81-4621-bb5f-09712327f37e49.MirrorCS"),sQuery(id+"F0.wireOp",EDGE,"7b8357ce-6b81-4621-bb5f-09712327f37e50.MirrorCS"),sQuery(id+"F0.wireOp",EDGE,"E62.MirrorCS"),sQuery(id+"F0.wireOp",EDGE,"7b8357ce-6b81-4621-bb5f-09712327f37e55.MirrorCS"),sQuery(id+"F0.wireOp",EDGE,"d83ce2ea-2607-4b6c-a04d-38c7ae4304c90.MirrorCS"),sQuery(id+"F0.wireOp",EDGE,"b69c18a7-e43b-42be-b145-92b5204aa2ed0.MirrorCS"),sQuery(id+"F0.wireOp",EDGE,"a0707623-7043-4475-b436-6124989390590.MirrorCS"),sQuery(id+"F0.wireOp",EDGE,"4f61c261-c1ce-4229-8802-2f54477ed9b20.MirrorCS"),sQuery(id+"F0.wireOp",EDGE,"PiAP6XZh-xq8d-wj9O-Epc7-kF4WUdjTUHBz"),sQuery(id+"F0.wireOp",EDGE,"26e37ba6-caeb-4f33-ab48-1d1fe7035cbd0.MirrorC"),sQuery(id+"F0.wireOp",EDGE,"2yan8IeJ-tOHB-Kgj5-MnLH-DyiSyil4pG3S"),sQuery(id+"F0.wireOp",EDGE,"gHJ05LQx-usyR-kV3a-hPzh-QXjW5T1wXW1p"),sQuery(id+"F0.wireOp",EDGE,"uchXSoDE-KjdM-uTwm-rJXX-9rzWfyOP3x4Z"),sQuery(id+"F0.wireOp",EDGE,"8eu2Gxre-rbZ0-mDo1-W97T-pc3IviFYihye"),sQuery(id+"F0.wireOp",EDGE,"eavqlNsN-eOFr-pDPr-DEgw-YRCTYlhg5u3t"),sQuery(id+"F0.wireOp",EDGE,"Bw8slYh4-NEub-OYFD-4ET6-0dd0G63bUOwi"),sQuery(id+"F0.wireOp",EDGE,"af94888a-cba0-45cd-aecc-a0270221dd82.trimOffspring"),sQuery(id+"F0.wireOp",EDGE,"36199e4a-d6a7-49c4-a502-27b3488fd5e6.filletArc"),sQuery(id+"F0.wireOp",EDGE,"9e30e6b1-65ef-4937-9bd8-18fed2c5f1090.MirrorCS"),sQuery(id+"F0.wireOp",EDGE,"31f30485-6f3e-4795-917b-55e225d339680.MirrorCS"),sQuery(id+"F0.wireOp",EDGE,"86aa6092-d3c3-42aa-99ce-90435510c5960.MirrorCS"),sQuery(id+"F0.wireOp",EDGE,"5a69975c-1d9b-4b23-809c-878e26df679d0.MirrorCS"),sQuery(id+"F0.wireOp",EDGE,"8025df49-7d22-4dba-957a-6396c4b11ce90.MirrorCS"),sQuery(id+"F0.wireOp",EDGE,"b23088bf-ab4c-4e44-9a43-da8ffa8499a00.MirrorCS"),sQuery(id+"F0.wireOp",EDGE,"d9780cfa-9ead-4347-a629-1b1a594d6e410.MirrorCS"),sQuery(id+"F0.wireOp",EDGE,"68fec51b-96b4-4918-b858-b07c475e679e0.MirrorCS"),sQuery(id+"F0.wireOp",EDGE,"b72a6ee6-5ab0-4ed6-be8f-ffada714514d0.MirrorCS"),sQuery(id+"F0.wireOp",EDGE,"8773bbf2-5ef2-485a-bde0-34addb67332b0.MirrorCS"),sQuery(id+"F0.wireOp",EDGE,"ce348970-fad1-4eb4-9c27-5204bf570fdb0.MirrorCS"),sQuery(id+"F0.wireOp",EDGE,"404c4f6d-7f85-4f91-8924-7a461248f6590.MirrorCS"),sQuery(id+"F0.wireOp",EDGE,"TJ6xSgkY-RBVc-ApbF-Rnxn-nYxT4uNRJTxX"),sQuery(id+"F0.wireOp",EDGE,"UOzbpYJr-Rpqu-ZeE8-tXKC-t89DSqlBGB8Q"),sQuery(id+"F0.wireOp",EDGE,"YxJJHRqV-amlc-LN3y-haml-tisoirnnfRJY"),sQuery(id+"F0.wireOp",EDGE,"033e0fe7-d3c1-42f5-ae8f-adbb043379e8.filletArc"),sQuery(id+"F0.wireOp",EDGE,"afa99035-e99d-4a73-974f-5500cdf2138a.filletArc"),sQuery(id+"F0.wireOp",EDGE,"9i3ea3iE-3Dll-Ek6R-PhGe-V1XcnAEkodY1.bottom"),sQuery(id+"F0.wireOp",EDGE,"9i3ea3iE-3Dll-Ek6R-PhGe-V1XcnAEkodY1.left"),sQuery(id+"F0.wireOp",EDGE,"9i3ea3iE-3Dll-Ek6R-PhGe-V1XcnAEkodY1.right"),sQuery(id+"F0.wireOp",EDGE,"1382622d-cae2-4c61-9f5c-b8746732d9fe0.MirrorCS"),sQuery(id+"F0.wireOp",EDGE,"0d70f9a0-c1ad-434e-a495-165a5a764f960.MirrorCS"),sQuery(id+"F0.wireOp",EDGE,"1f8d5036-162d-4fc3-b441-7a8ab5cd179e0.MirrorCS"),sQuery(id+"F0.wireOp",EDGE,"Km0E7gO1-P8tX-SnyZ-vo1L-W35BEzFtr7vK"),sQuery(id+"F0.wireOp",EDGE,"4twT0r3F-PA9R-wz1e-iyg0-9RBk79VGwi7g"),sQuery(id+"F0.wireOp",EDGE,"14bccf5c-bb99-48c5-a73f-577480a40b4e0.MirrorCS"),sQuery(id+"F0.wireOp",EDGE,"a123c59d-a695-4b06-9137-5aaff9e2b4be0.MirrorCS"),sQuery(id+"F0.wireOp",EDGE,"E68"),sQuery(id+"F0.wireOp",EDGE,"E69.MirrorC"),sQuery(id+"F0.wireOp",EDGE,"E70.MirrorC"),sQuery(id+"F0.wireOp",EDGE,"E71.MirrorC")])],"isStart":false});
            var sketch = newSketch(context, id + "F6", { "sketchPlane" : qUnion([Q0])});
            skLineSegment(sketch, "E176.bottom", {"start": v(-6, 43.5) * mm, "end": v(6, 43.5) * mm});
            skLineSegment(sketch, "E176.top", {"start": v(-6, 35.5) * mm, "end": v(6, 35.5) * mm});
            skLineSegment(sketch, "E176.left", {"start": v(-8, 41.5) * mm, "end": v(-8, 37.5) * mm});
            skLineSegment(sketch, "E176.right", {"start": v(8, 41.5) * mm, "end": v(8, 37.5) * mm});
            skPoint(sketch, "E177.visualSharp", {"position": v(-8, 43.5) * mm});
            skArc(sketch, "E177.filletArc", {"start": v(-6, 43.5) * mm, "mid": v(-7.41, 42.91) * mm, "end": v(-8, 41.5) * mm});
            skPoint(sketch, "E178.visualSharp", {"position": v(-8, 35.5) * mm});
            skArc(sketch, "E178.filletArc", {"start": v(-8, 37.5) * mm, "mid": v(-7.41, 36.09) * mm, "end": v(-6, 35.5) * mm});
            skPoint(sketch, "E179.visualSharp", {"position": v(8, 35.5) * mm});
            skArc(sketch, "E179.filletArc", {"start": v(6, 35.5) * mm, "mid": v(7.41, 36.09) * mm, "end": v(8, 37.5) * mm});
            skPoint(sketch, "E180.visualSharp", {"position": v(8, 43.5) * mm});
            skArc(sketch, "E180.filletArc", {"start": v(8, 41.5) * mm, "mid": v(7.41, 42.91) * mm, "end": v(6, 43.5) * mm});
            skLineSegment(sketch, "E181", {"start": v(-5, -28) * mm, "end": v(-5, -31) * mm, "construction": true});
            skLineSegment(sketch, "E182.MirrorCS", {"start": v(5, -28) * mm, "end": v(5, -31) * mm, "construction": true});
            skArc(sketch, "E183.0.startCap", {"start": v(-6.5, -28) * mm, "mid": v(-5, -26.5) * mm, "end": v(-3.5, -28) * mm});
            skArc(sketch, "E183.0.endCap", {"start": v(-3.5, -31) * mm, "mid": v(-5, -32.5) * mm, "end": v(-6.5, -31) * mm});
            skLineSegment(sketch, "E183.0.left", {"start": v(-3.5, -28) * mm, "end": v(-3.5, -31) * mm});
            skLineSegment(sketch, "E183.0.right", {"start": v(-6.5, -28) * mm, "end": v(-6.5, -31) * mm});
            skArc(sketch, "E183.1.startCap", {"start": v(3.5, -28) * mm, "mid": v(5, -26.5) * mm, "end": v(6.5, -28) * mm});
            skArc(sketch, "E183.1.endCap", {"start": v(6.5, -31) * mm, "mid": v(5, -32.5) * mm, "end": v(3.5, -31) * mm});
            skLineSegment(sketch, "E183.1.left", {"start": v(6.5, -28) * mm, "end": v(6.5, -31) * mm});
            skLineSegment(sketch, "E183.1.right", {"start": v(3.5, -28) * mm, "end": v(3.5, -31) * mm});
            skCircle(sketch, "E184", {"center": v(0, 0) * mm, "radius": 9 * mm});
            skSolve(sketch);
        }
        {
            var Q0;
            Q0=qSketchRegion(id+"F6",true);
            extrude(context, id + "F7", {"entities" : qUnion([Q0]), "operationType" : NewBodyOperationType.REMOVE, "oppositeDirection" : true, "depth" : 25 * mm, "offsetDistance" : 25 * mm});
        }
        {
            var Q0;
            Q0=makeQuery(id+"F1.opExtrude","SWEPT_EDGE",EDGE,{"disambiguationData":[OSD([sQuery(id+"F0.wireOp",EDGE,"E6"),sQuery(id+"F0.wireOp",EDGE,"E86")])]});
            var Q1;
            Q1=makeQuery(id+"F1.opExtrude","SWEPT_EDGE",EDGE,{"disambiguationData":[OSD([sQuery(id+"F0.wireOp",EDGE,"E26.MirrorCS"),sQuery(id+"F0.wireOp",EDGE,"E87")])]});
            fillet(context, id + "F8", {"entities" : qUnion([Q0, Q1]), "radius" : 3 * mm, "tangentPropagation" : true, "allowEdgeOverflow" : false});
        }
        {
            var Q0;
            Q0=makeQuery(id+"F1.opExtrude","CAP_FACE",FACE,{"disambiguationData":[OSD([sQuery(id+"F0.wireOp",EDGE,"E0"),sQuery(id+"F0.wireOp",EDGE,"E5.bottom"),sQuery(id+"F0.wireOp",EDGE,"E5.left"),sQuery(id+"F0.wireOp",EDGE,"E5.right"),sQuery(id+"F0.wireOp",EDGE,"E6"),sQuery(id+"F0.wireOp",EDGE,"E7"),sQuery(id+"F0.wireOp",EDGE,"E8"),sQuery(id+"F0.wireOp",EDGE,"E10.0.startCap"),sQuery(id+"F0.wireOp",EDGE,"E10.0.endCap"),sQuery(id+"F0.wireOp",EDGE,"E10.0.left"),sQuery(id+"F0.wireOp",EDGE,"E10.0.right"),sQuery(id+"F0.wireOp",EDGE,"E11.filletArc"),sQuery(id+"F0.wireOp",EDGE,"E12.filletArc"),sQuery(id+"F0.wireOp",EDGE,"E13.filletArc"),sQuery(id+"F0.wireOp",EDGE,"E14.filletArc"),sQuery(id+"F0.wireOp",EDGE,"E15.MirrorCS"),sQuery(id+"F0.wireOp",EDGE,"E16.MirrorCS"),sQuery(id+"F0.wireOp",EDGE,"E17.MirrorCS"),sQuery(id+"F0.wireOp",EDGE,"E18.MirrorCS"),sQuery(id+"F0.wireOp",EDGE,"E19.MirrorCS"),sQuery(id+"F0.wireOp",EDGE,"E20.MirrorCS"),sQuery(id+"F0.wireOp",EDGE,"E21.MirrorCS"),sQuery(id+"F0.wireOp",EDGE,"E22.MirrorCS"),sQuery(id+"F0.wireOp",EDGE,"E23.MirrorCS"),sQuery(id+"F0.wireOp",EDGE,"E24.MirrorCS"),sQuery(id+"F0.wireOp",EDGE,"E26.MirrorCS"),sQuery(id+"F0.wireOp",EDGE,"E27.MirrorC"),sQuery(id+"F0.wireOp",EDGE,"E29.MirrorCS"),sQuery(id+"F0.wireOp",EDGE,"E33.MirrorCS"),sQuery(id+"F0.wireOp",EDGE,"E34.MirrorCS"),sQuery(id+"F0.wireOp",EDGE,"E38.MirrorCS"),sQuery(id+"F0.wireOp",EDGE,"E39.MirrorCS"),sQuery(id+"F0.wireOp",EDGE,"E40.MirrorCS"),sQuery(id+"F0.wireOp",EDGE,"E41.MirrorCS"),sQuery(id+"F0.wireOp",EDGE,"E42.MirrorCS"),sQuery(id+"F0.wireOp",EDGE,"E43.MirrorCS"),sQuery(id+"F0.wireOp",EDGE,"E44.MirrorCS"),sQuery(id+"F0.wireOp",EDGE,"E45.MirrorCS"),sQuery(id+"F0.wireOp",EDGE,"E46.MirrorCS"),sQuery(id+"F0.wireOp",EDGE,"E47.MirrorCS"),sQuery(id+"F0.wireOp",EDGE,"E48.MirrorCS"),sQuery(id+"F0.wireOp",EDGE,"E49.MirrorCS"),sQuery(id+"F0.wireOp",EDGE,"E50.MirrorC"),sQuery(id+"F0.wireOp",EDGE,"E51.MirrorC"),sQuery(id+"F0.wireOp",EDGE,"E53.MirrorCS"),sQuery(id+"F0.wireOp",EDGE,"E55.MirrorCS"),sQuery(id+"F0.wireOp",EDGE,"E58.MirrorCS"),sQuery(id+"F0.wireOp",EDGE,"E59.MirrorCS"),sQuery(id+"F0.wireOp",EDGE,"E60.MirrorCS"),sQuery(id+"F0.wireOp",EDGE,"E62.MirrorCS"),sQuery(id+"F0.wireOp",EDGE,"PiAP6XZh-xq8d-wj9O-Epc7-kF4WUdjTUHBz"),sQuery(id+"F0.wireOp",EDGE,"E68"),sQuery(id+"F0.wireOp",EDGE,"E69.MirrorC"),sQuery(id+"F0.wireOp",EDGE,"E70.MirrorC"),sQuery(id+"F0.wireOp",EDGE,"E71.MirrorC"),sQuery(id+"F0.wireOp",EDGE,"saBew1CV-SxRc-ZB9K-e4XU-TCJo4jc1kgwB"),sQuery(id+"F0.wireOp",EDGE,"As7GNjuw-uwTQ-EC8a-4VWo-RmuX3ZlHdixJ"),sQuery(id+"F0.wireOp",EDGE,"17ac02e8-9e55-49a8-8953-3050a0e1ff9d.trimOffspring"),sQuery(id+"F0.wireOp",EDGE,"fgNwwMFg-OnY8-yskJ-sLJ1-vSz1G99tKk8o"),sQuery(id+"F0.wireOp",EDGE,"jiS4iSMn-SGWw-wNEF-CNbn-W2Xm5X2EO89s"),sQuery(id+"F0.wireOp",EDGE,"a3419795-80d2-4dbb-87c2-bbe54f5cbc13.trimOffspring"),sQuery(id+"F0.wireOp",EDGE,"2f9ed6c8-7ab2-4140-a752-6b7fb87077802.MirrorCS"),sQuery(id+"F0.wireOp",EDGE,"2f9ed6c8-7ab2-4140-a752-6b7fb87077807.MirrorCS"),sQuery(id+"F0.wireOp",EDGE,"2f9ed6c8-7ab2-4140-a752-6b7fb87077808.MirrorCS"),sQuery(id+"F0.wireOp",EDGE,"2f9ed6c8-7ab2-4140-a752-6b7fb870778010.MirrorCS"),sQuery(id+"F0.wireOp",EDGE,"2f9ed6c8-7ab2-4140-a752-6b7fb870778011.MirrorCS"),sQuery(id+"F0.wireOp",EDGE,"2f9ed6c8-7ab2-4140-a752-6b7fb870778012.MirrorCS"),sQuery(id+"F0.wireOp",EDGE,"2f9ed6c8-7ab2-4140-a752-6b7fb870778014.MirrorCS"),sQuery(id+"F0.wireOp",EDGE,"E72"),sQuery(id+"F0.wireOp",EDGE,"E73.MirrorCS"),sQuery(id+"F0.wireOp",EDGE,"E74.MirrorCS"),sQuery(id+"F0.wireOp",EDGE,"E75.MirrorCS"),sQuery(id+"F0.wireOp",EDGE,"E76.trimOffspring"),sQuery(id+"F0.wireOp",EDGE,"E77.MirrorCS"),sQuery(id+"F0.wireOp",EDGE,"E78.MirrorCS"),sQuery(id+"F0.wireOp",EDGE,"E79.MirrorCS"),sQuery(id+"F0.wireOp",EDGE,"E80"),sQuery(id+"F0.wireOp",EDGE,"E81.filletArc"),sQuery(id+"F0.wireOp",EDGE,"E82.filletArc"),sQuery(id+"F0.wireOp",EDGE,"E83.filletArc"),sQuery(id+"F0.wireOp",EDGE,"E84.filletArc"),sQuery(id+"F0.wireOp",EDGE,"E85"),sQuery(id+"F0.wireOp",EDGE,"E86"),sQuery(id+"F0.wireOp",EDGE,"E87"),sQuery(id+"F0.wireOp",EDGE,"E88.filletArc"),sQuery(id+"F0.wireOp",EDGE,"E89.filletArc"),sQuery(id+"F0.wireOp",EDGE,"E90.MirrorC"),sQuery(id+"F0.wireOp",EDGE,"E91.filletArc"),sQuery(id+"F0.wireOp",EDGE,"E92.filletArc")])],"isStart":false});
            var sketch = newSketch(context, id + "F9", { "sketchPlane" : qUnion([Q0])});
            skLineSegment(sketch, "E185", {"start": v(-104.04, -93.68) * mm, "end": v(0, -12) * mm, "construction": true});
            skLineSegment(sketch, "E186", {"start": v(-104.04, -93.68) * mm, "end": v(-116.63, -103.56) * mm, "construction": true});
            skLineSegment(sketch, "E187", {"start": v(-104.04, 93.68) * mm, "end": v(0, 12) * mm, "construction": true});
            skArc(sketch, "E188", {"start": v(-29.02, 36.04) * mm, "mid": v(-23.8, 33.12) * mm, "end": v(-18.53, 30.27) * mm});
            skArc(sketch, "E189.MirrorCS", {"start": v(-30.24, 34.48) * mm, "mid": v(-24.95, 28.77) * mm, "end": v(-19.75, 22.97) * mm});
            skLineSegment(sketch, "E190", {"start": v(-18, 29.38) * mm, "end": v(-18, 23.64) * mm});
            skPoint(sketch, "E191.visualSharp", {"position": v(-35, 39.48) * mm});
            skArc(sketch, "E191.filletArc", {"start": v(-29.02, 36.04) * mm, "mid": v(-30.3, 35.78) * mm, "end": v(-30.24, 34.48) * mm});
            skPoint(sketch, "E192.visualSharp", {"position": v(-18, 29.98) * mm});
            skArc(sketch, "E192.filletArc", {"start": v(-18, 29.38) * mm, "mid": v(-18.14, 29.9) * mm, "end": v(-18.53, 30.27) * mm});
            skPoint(sketch, "E193.visualSharp", {"position": v(-18, 20.98) * mm});
            skArc(sketch, "E193.filletArc", {"start": v(-19.75, 22.97) * mm, "mid": v(-18.65, 22.7) * mm, "end": v(-18, 23.64) * mm});
            skArc(sketch, "E194.MirrorCS", {"start": v(18, 29.38) * mm, "mid": v(18.14, 29.9) * mm, "end": v(18.53, 30.27) * mm});
            skArc(sketch, "E195.MirrorCS", {"start": v(19.75, 22.97) * mm, "mid": v(18.65, 22.7) * mm, "end": v(18, 23.64) * mm});
            skArc(sketch, "E196.MirrorCS", {"start": v(29.02, 36.04) * mm, "mid": v(30.3, 35.78) * mm, "end": v(30.24, 34.48) * mm});
            skPoint(sketch, "E197.MirrorP", {"position": v(18, 20.98) * mm});
            skArc(sketch, "E198.MirrorCS", {"start": v(29.02, 36.04) * mm, "mid": v(23.8, 33.12) * mm, "end": v(18.53, 30.27) * mm});
            skPoint(sketch, "E199.MirrorP", {"position": v(18, 29.98) * mm});
            skArc(sketch, "E200.MirrorCS", {"start": v(30.24, 34.48) * mm, "mid": v(24.95, 28.77) * mm, "end": v(19.75, 22.97) * mm});
            skLineSegment(sketch, "E201.MirrorCS", {"start": v(18, 29.38) * mm, "end": v(18, 23.64) * mm});
            skArc(sketch, "E202.MirrorCS", {"start": v(18, -29.38) * mm, "mid": v(18.14, -29.9) * mm, "end": v(18.53, -30.27) * mm});
            skArc(sketch, "E203.MirrorCS", {"start": v(29.02, -36.04) * mm, "mid": v(30.3, -35.78) * mm, "end": v(30.24, -34.48) * mm});
            skArc(sketch, "E204.MirrorCS", {"start": v(19.75, -22.97) * mm, "mid": v(18.65, -22.7) * mm, "end": v(18, -23.64) * mm});
            skPoint(sketch, "E205.MirrorP", {"position": v(18, -29.98) * mm});
            skLineSegment(sketch, "E206.MirrorCS", {"start": v(18, -29.38) * mm, "end": v(18, -23.64) * mm});
            skPoint(sketch, "E207.MirrorP", {"position": v(18, -20.98) * mm});
            skArc(sketch, "E208.MirrorCS", {"start": v(29.02, -36.04) * mm, "mid": v(23.8, -33.12) * mm, "end": v(18.53, -30.27) * mm});
            skArc(sketch, "E209.MirrorCS", {"start": v(30.24, -34.48) * mm, "mid": v(24.95, -28.77) * mm, "end": v(19.75, -22.97) * mm});
            skArc(sketch, "E210.MirrorCS", {"start": v(-18, -29.38) * mm, "mid": v(-18.14, -29.9) * mm, "end": v(-18.53, -30.27) * mm});
            skArc(sketch, "E211.MirrorCS", {"start": v(-19.75, -22.97) * mm, "mid": v(-18.65, -22.7) * mm, "end": v(-18, -23.64) * mm});
            skArc(sketch, "E212.MirrorCS", {"start": v(-29.02, -36.04) * mm, "mid": v(-30.3, -35.78) * mm, "end": v(-30.24, -34.48) * mm});
            skArc(sketch, "E213.MirrorCS", {"start": v(-30.24, -34.48) * mm, "mid": v(-24.95, -28.77) * mm, "end": v(-19.75, -22.97) * mm});
            skPoint(sketch, "E214.MirrorP", {"position": v(-18, -29.98) * mm});
            skArc(sketch, "E215.MirrorCS", {"start": v(-29.02, -36.04) * mm, "mid": v(-23.8, -33.12) * mm, "end": v(-18.53, -30.27) * mm});
            skLineSegment(sketch, "E216.MirrorCS", {"start": v(-18, -29.38) * mm, "end": v(-18, -23.64) * mm});
            skPoint(sketch, "E217.MirrorP", {"position": v(-18, -20.98) * mm});
            skSolve(sketch);
        }
        {
            var Q0;
            Q0=qSketchRegion(id+"F9",true);
            extrude(context, id + "F10", {"entities" : qUnion([Q0]), "operationType" : NewBodyOperationType.REMOVE, "oppositeDirection" : true, "depth" : 25 * mm, "offsetDistance" : 25 * mm});
        }
    });
